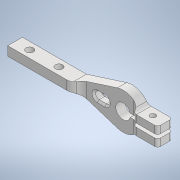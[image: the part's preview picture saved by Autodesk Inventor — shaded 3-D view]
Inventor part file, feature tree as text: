
AUTODESK INVENTOR PART (.ipt)
format: ipt  version: 2020 (Build 240168000, 168)  size: 287,744 bytes
history: native  units: mm
features: extrude x9, sketch x9, projected_geometry x8, fillet x6, other x4, chamfer x1, reference x1
ambient origin geometry x8: Origin, YZ Plane, XZ Plane, XY Plane, X Axis, Y Axis, Z Axis, Center Point
bodies: Solid1 (feature_tree)
feature tree (38):
  extrude  "Extrusion1"  Depth=8.0mm
  extrude  "Extrusion2"  Depth=2.5mm
  extrude  "Extrusion3"  Depth=5.0mm
  extrude  "Extrusion4"  Depth=5.0mm
  extrude  "Extrusion5"  Depth=2.0mm
  extrude  "Extrusion6"  Depth=4.0mm
  fillet  "Fillet1"  Radius=4.0mm
  extrude  "Extrusion7"  Depth=4.0mm
  fillet  "Fillet2"  Radius=5.0mm
  fillet  "Fillet3"  Radius=8.0mm
  fillet  "Fillet4"  Radius=4.0mm
  fillet  "Fillet5"  Radius=4.0mm
  extrude  "Extrusion8"  Depth=10.0mm TaperAngle=0.0deg
  extrude  "Extrusion9"  Depth=2.0mm
  fillet  "Fillet6"  Radius=8.0mm
  chamfer  "Chamfer1"  Distance=5.0mm
  sketch  "Sketch1"  dims[d0=8.0mm d1=60.0mm]
  reference  "Reference1"
  sketch  "Sketch2"  dims[d2=20.0mm d3=2.5mm]
  projected_geometry  "Projected Loop1"
  sketch  "Sketch3"  dims[d4=35.0mm d5=5.0mm]
  projected_geometry  "Projected Loop2"
  sketch  "Sketch4"  dims[d6=5.0mm d7=0.0mm d8=7.6mm]
  projected_geometry  "Projected Loop3"
  sketch  "Sketch5"  dims[d9=2.0mm d10=12.0mm]
  projected_geometry  "Projected Loop4"
  sketch  "Sketch6"  dims[d11=5.0mm d12=0.0mm d13=18.0mm d14=4.0mm]
  projected_geometry  "Projected Loop5"
  sketch  "Sketch7"  dims[d15=18.0mm d16=4.0mm d17=5.0mm d18=0.0mm d19=8.0mm d20=4.0mm d21=0.0mm d22=4.0mm d23=0.0mm]
  projected_geometry  "Projected Loop6"
  sketch  "Sketch8"  dims[d24=3.0mm d25=10.0mm d26=0.0mm]
  projected_geometry  "Projected Loop7"
  sketch  "Sketch9"  dims[d27=3.0mm d28=35.0mm d29=8.0mm d30=5.0mm d31=0.0mm d32=6.0mm d33=1.5mm d34=3.0mm d35=2.0mm d36=12.0mm d37=2.0mm d38=4.0mm d39=5.0mm d40=0.0mm d41=8.0mm d42=16.0mm d43=4.0mm d44=4.0mm d45=5.0mm d46=0.0mm d47=6.0mm d48=1.0mm d49=2.0mm d50=45.0deg]
  projected_geometry  "Projected Loop8"
  parser-record x1  (decoder bookkeeping rows leaked as tree rows — omitted from the tree; the rows remain in map.json)
  other  "delta_1.iam"
  other  "arm_shift_1:3"
  other  "pin_8_45:1"
note: 1 file-system path scrubbed to <path> (originals preserved in map.json)
